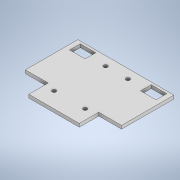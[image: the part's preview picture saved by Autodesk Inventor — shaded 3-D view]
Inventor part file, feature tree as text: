
AUTODESK INVENTOR PART (.ipt)
format: ipt  version: 2021 (Build 250183000, 183)  size: 137,216 bytes
history: native  units: mm
features: other x1, extrude x1, sketch x1
ambient origin geometry x8: Origin, YZ Plane, XZ Plane, XY Plane, X Axis, Y Axis, Z Axis, Center Point
bodies: Body1 (feature_tree)
feature tree (3):
  other  "Sólido1"
  extrude  "Extrusión1"  Depth=99.0mm
  sketch  "Boceto1"  dims[d0=54.0mm d1=99.0mm d2=20.0mm d3=52.0mm d4=23.5mm d5=23.5mm d6=4.0mm d7=16.0mm d8=10.0mm d9=2.5mm d10=5.0mm d11=11.0mm d12=16.0mm d13=4.0mm d15=9.5mm d16=3.4mm d17=0.0mm d18=36.0mm d19=17.0mm]
